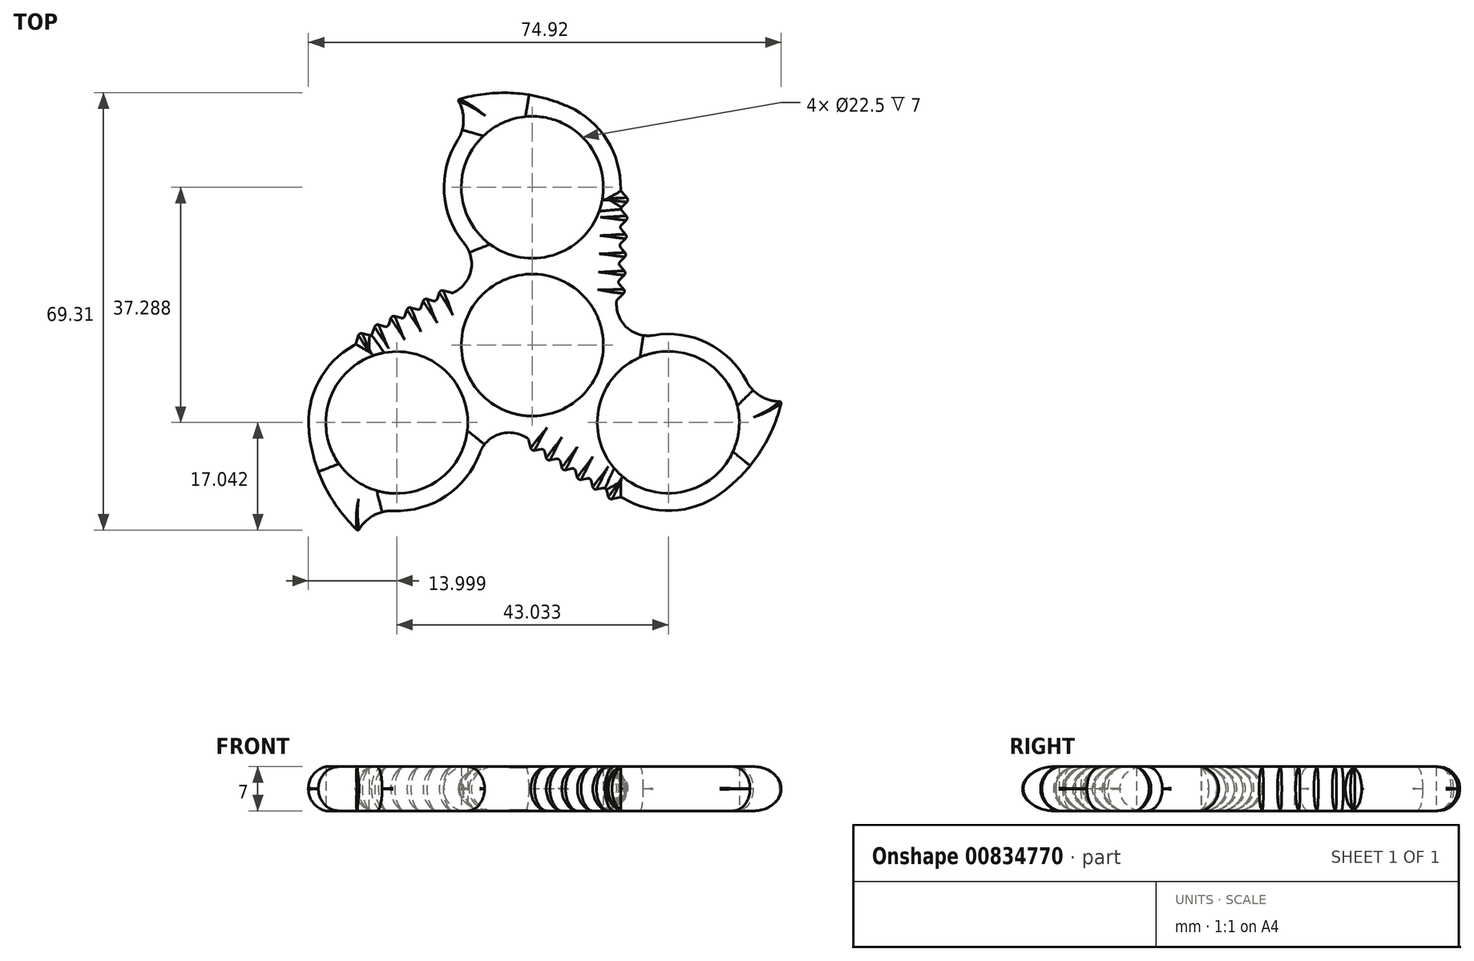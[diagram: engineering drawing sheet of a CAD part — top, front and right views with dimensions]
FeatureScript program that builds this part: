
annotation { "Feature Type Name" : "Feature", "Feature Type Description" : "" }
export const myFeature = defineFeature(function(context is Context, id is Id, definition is map)
    precondition{}
    {
        {
            var Q0;
            Q0=qCreatedBy(makeId("Top.planeOp"),FACE);
            var sketch = newSketch(context, id + "F0", { "sketchPlane" : qUnion([Q0])});
            skCircle(sketch, "E0", {"center": v(0, 0) * mm, "radius": 25 * mm, "construction": true});
            skCircle(sketch, "E1", {"center": v(0, 0) * mm, "radius": 11.25 * mm});
            skArc(sketch, "E2", {"start": v(14, 24.5) * mm, "mid": v(11.9, 32.39) * mm, "end": v(5.75, 37.77) * mm});
            skLineSegment(sketch, "E3", {"start": v(13.35, 6.66) * mm, "end": v(13.36, 7.1) * mm});
            skPoint(sketch, "E4.visualSharp", {"position": v(-4.7, 11.81) * mm});
            skArc(sketch, "E4.filletArc", {"start": v(-12.27, 8.44) * mm, "mid": v(-9.7, 11.89) * mm, "end": v(-10.77, 16.05) * mm});
            skPoint(sketch, "E5.visualSharp", {"position": v(13.05, -1.63) * mm});
            skArc(sketch, "E6", {"start": v(5.75, 37.77) * mm, "mid": v(-2.94, 39.93) * mm, "end": v(-11.83, 38.9) * mm});
            skArc(sketch, "E7", {"start": v(-11.83, 32.48) * mm, "mid": v(-10.9, 35.7) * mm, "end": v(-11.83, 38.9) * mm});
            skArc(sketch, "E8.trimOffspring", {"start": v(-11.83, 32.48) * mm, "mid": v(-13.97, 24.1) * mm, "end": v(-10.77, 16.05) * mm});
            skLineSegment(sketch, "E9", {"start": v(14, 24.5) * mm, "end": v(15.31, 23) * mm});
            skLineSegment(sketch, "E10", {"start": v(15.31, 23) * mm, "end": v(13.89, 21.6) * mm});
            skLineSegment(sketch, "E11.1.0.0", {"start": v(15.2, 20.1) * mm, "end": v(13.78, 18.7) * mm});
            skLineSegment(sketch, "E11.1.0.1", {"start": v(13.89, 21.6) * mm, "end": v(15.2, 20.1) * mm});
            skLineSegment(sketch, "E11.2.0.0", {"start": v(15.1, 17.2) * mm, "end": v(13.68, 15.8) * mm});
            skLineSegment(sketch, "E11.2.0.1", {"start": v(13.78, 18.7) * mm, "end": v(15.1, 17.2) * mm});
            skLineSegment(sketch, "E11.3.0.0", {"start": v(15, 14.3) * mm, "end": v(13.57, 12.9) * mm});
            skLineSegment(sketch, "E11.3.0.1", {"start": v(13.68, 15.8) * mm, "end": v(15, 14.3) * mm});
            skLineSegment(sketch, "E11.4.0.0", {"start": v(14.9, 11.4) * mm, "end": v(13.47, 10) * mm});
            skLineSegment(sketch, "E11.4.0.1", {"start": v(13.57, 12.9) * mm, "end": v(14.9, 11.4) * mm});
            skLineSegment(sketch, "E11.5.0.0", {"start": v(14.79, 8.5) * mm, "end": v(13.36, 7.1) * mm});
            skLineSegment(sketch, "E11.5.0.1", {"start": v(13.47, 10) * mm, "end": v(14.79, 8.5) * mm});
            skArc(sketch, "E12.1.0", {"start": v(-22.04, -26.28) * mm, "mid": v(-25.29, -27.08) * mm, "end": v(-27.6, -29.49) * mm});
            skArc(sketch, "E12.1.1", {"start": v(-1, -14.64) * mm, "mid": v(-5.27, -14.14) * mm, "end": v(-8.35, -17.14) * mm});
            skArc(sketch, "E12.1.2", {"start": v(-22.04, -26.28) * mm, "mid": v(-13.71, -23.93) * mm, "end": v(-8.35, -17.14) * mm});
            skArc(sketch, "E12.1.3", {"start": v(-35.41, -13.7) * mm, "mid": v(-32.94, -22.3) * mm, "end": v(-27.6, -29.49) * mm});
            skArc(sketch, "E12.1.4", {"start": v(-28.04, 0.08) * mm, "mid": v(-33.82, -5.68) * mm, "end": v(-35.41, -13.7) * mm});
            skLineSegment(sketch, "E12.1.6", {"start": v(-28.04, 0.08) * mm, "end": v(-27.4, 1.98) * mm});
            skLineSegment(sketch, "E12.1.7", {"start": v(-27.4, 1.98) * mm, "end": v(-25.47, 1.44) * mm});
            skLineSegment(sketch, "E12.1.8", {"start": v(-25.48, 1.44) * mm, "end": v(-24.84, 3.34) * mm});
            skLineSegment(sketch, "E12.1.9", {"start": v(-24.84, 3.34) * mm, "end": v(-22.91, 2.8) * mm});
            skLineSegment(sketch, "E12.1.10", {"start": v(-22.91, 2.8) * mm, "end": v(-22.28, 4.7) * mm});
            skLineSegment(sketch, "E12.1.11", {"start": v(-22.28, 4.7) * mm, "end": v(-20.35, 4.16) * mm});
            skLineSegment(sketch, "E12.1.12", {"start": v(-20.35, 4.16) * mm, "end": v(-19.71, 6.05) * mm});
            skLineSegment(sketch, "E12.1.13", {"start": v(-19.71, 6.05) * mm, "end": v(-17.79, 5.52) * mm});
            skLineSegment(sketch, "E12.1.14", {"start": v(-17.79, 5.51) * mm, "end": v(-17.15, 7.41) * mm});
            skLineSegment(sketch, "E12.1.15", {"start": v(-17.15, 7.41) * mm, "end": v(-15.23, 6.87) * mm});
            skLineSegment(sketch, "E12.1.16", {"start": v(-15.23, 6.87) * mm, "end": v(-14.59, 8.77) * mm});
            skLineSegment(sketch, "E12.1.17", {"start": v(-14.59, 8.77) * mm, "end": v(-12.66, 8.23) * mm});
            skLineSegment(sketch, "E12.1.18", {"start": v(-12.27, 8.44) * mm, "end": v(-12.66, 8.23) * mm});
            skArc(sketch, "E12.2.0", {"start": v(33.95, -5.74) * mm, "mid": v(36.26, -8.15) * mm, "end": v(39.5, -8.95) * mm});
            skArc(sketch, "E12.2.1", {"start": v(13.35, 6.66) * mm, "mid": v(15.05, 2.72) * mm, "end": v(19.19, 1.55) * mm});
            skArc(sketch, "E12.2.2", {"start": v(33.95, -5.74) * mm, "mid": v(27.75, 0.3) * mm, "end": v(19.19, 1.55) * mm});
            skArc(sketch, "E12.2.3", {"start": v(29.73, -23.6) * mm, "mid": v(35.95, -17.16) * mm, "end": v(39.5, -8.95) * mm});
            skArc(sketch, "E12.2.4", {"start": v(14.12, -24.11) * mm, "mid": v(22, -26.24) * mm, "end": v(29.73, -23.6) * mm});
            skLineSegment(sketch, "E12.2.6", {"start": v(14.12, -24.11) * mm, "end": v(12.16, -24.5) * mm});
            skLineSegment(sketch, "E12.2.7", {"start": v(12.16, -24.5) * mm, "end": v(11.66, -22.57) * mm});
            skLineSegment(sketch, "E12.2.8", {"start": v(11.66, -22.57) * mm, "end": v(9.7, -22.97) * mm});
            skLineSegment(sketch, "E12.2.9", {"start": v(9.7, -22.97) * mm, "end": v(9.2, -21.03) * mm});
            skLineSegment(sketch, "E12.2.10", {"start": v(9.2, -21.03) * mm, "end": v(7.24, -21.43) * mm});
            skLineSegment(sketch, "E12.2.11", {"start": v(7.24, -21.43) * mm, "end": v(6.74, -19.5) * mm});
            skLineSegment(sketch, "E12.2.12", {"start": v(6.75, -19.5) * mm, "end": v(4.79, -19.89) * mm});
            skLineSegment(sketch, "E12.2.13", {"start": v(4.79, -19.89) * mm, "end": v(4.29, -17.95) * mm});
            skLineSegment(sketch, "E12.2.14", {"start": v(4.29, -17.95) * mm, "end": v(2.33, -18.35) * mm});
            skLineSegment(sketch, "E12.2.15", {"start": v(2.33, -18.35) * mm, "end": v(1.83, -16.41) * mm});
            skLineSegment(sketch, "E12.2.16", {"start": v(1.83, -16.41) * mm, "end": v(-0.13, -16.8) * mm});
            skLineSegment(sketch, "E12.2.17", {"start": v(-0.13, -16.8) * mm, "end": v(-0.63, -14.87) * mm});
            skLineSegment(sketch, "E12.2.18", {"start": v(-1, -14.64) * mm, "end": v(-0.63, -14.87) * mm});
            skPoint(sketch, "E12.center", {"position": v(0.03, -3.97) * mm});
            skLineSegment(sketch, "E13.trimOffspring", {"start": v(-25.47, 1.44) * mm, "end": v(-25.48, 1.44) * mm});
            skLineSegment(sketch, "E14.trimOffspring", {"start": v(-22.91, 2.8) * mm, "end": v(-22.91, 2.8) * mm});
            skLineSegment(sketch, "E15.trimOffspring", {"start": v(-20.35, 4.16) * mm, "end": v(-20.35, 4.16) * mm});
            skLineSegment(sketch, "E16.trimOffspring", {"start": v(-17.79, 5.52) * mm, "end": v(-17.79, 5.51) * mm});
            skLineSegment(sketch, "E17.trimOffspring", {"start": v(-15.23, 6.87) * mm, "end": v(-15.23, 6.87) * mm});
            skLineSegment(sketch, "E18.trimOffspring", {"start": v(1.83, -16.41) * mm, "end": v(1.83, -16.41) * mm});
            skLineSegment(sketch, "E19.trimOffspring", {"start": v(4.29, -17.95) * mm, "end": v(4.29, -17.95) * mm});
            skLineSegment(sketch, "E20.trimOffspring", {"start": v(6.74, -19.5) * mm, "end": v(6.75, -19.5) * mm});
            skLineSegment(sketch, "E21.trimOffspring", {"start": v(9.2, -21.03) * mm, "end": v(9.2, -21.03) * mm});
            skLineSegment(sketch, "E22.trimOffspring", {"start": v(11.26, -22.32) * mm, "end": v(11.66, -22.57) * mm});
            skLineSegment(sketch, "E23.trimOffspring", {"start": v(13.47, 10) * mm, "end": v(13.47, 10) * mm});
            skLineSegment(sketch, "E24.trimOffspring", {"start": v(13.57, 12.9) * mm, "end": v(13.57, 12.9) * mm});
            skLineSegment(sketch, "E25.trimOffspring", {"start": v(13.68, 15.8) * mm, "end": v(13.68, 15.8) * mm});
            skLineSegment(sketch, "E26.trimOffspring", {"start": v(13.78, 18.7) * mm, "end": v(13.78, 18.7) * mm});
            skLineSegment(sketch, "E27.trimOffspring", {"start": v(13.78, 18.7) * mm, "end": v(13.78, 18.7) * mm, "construction": true});
            skLineSegment(sketch, "E28.trimOffspring", {"start": v(13.89, 21.6) * mm, "end": v(13.89, 21.6) * mm});
            skPoint(sketch, "E29.0.midPoint", {"position": v(13.99, -7.94) * mm});
            skLineSegment(sketch, "E30", {"start": v(0.03, -3.97) * mm, "end": v(0, 25) * mm});
            skCircle(sketch, "E31", {"center": v(-21.48, -12.29) * mm, "radius": 11.25 * mm});
            skCircle(sketch, "E32", {"center": v(0, 25) * mm, "radius": 11.25 * mm});
            skCircle(sketch, "E33", {"center": v(21.55, -12.25) * mm, "radius": 11.25 * mm});
            skSolve(sketch);
        }
        {
            var Q0;
            Q0=qSketchRegion(id+"F0",true);
            extrude(context, id + "F1", {"entities" : qUnion([Q0]), "depth" : 7 * mm, "offsetDistance" : 25 * mm});
        }
        {
            var Q0;
            Q0=makeQuery(id+"F1.opExtrude","SWEPT_EDGE",EDGE,{"disambiguationData":[OSD([sQuery(id+"F0.wireOp",EDGE,"E12.1.17"),sQuery(id+"F0.wireOp",EDGE,"E12.1.18")])]});
            var Q1;
            Q1=makeQuery(id+"F1.opExtrude","SWEPT_EDGE",EDGE,{"disambiguationData":[OSD([sQuery(id+"F0.wireOp",EDGE,"E12.1.16"),sQuery(id+"F0.wireOp",EDGE,"E12.1.17")])]});
            var Q2;
            Q2=makeQuery(id+"F1.opExtrude","SWEPT_EDGE",EDGE,{"disambiguationData":[OSD([sQuery(id+"F0.wireOp",EDGE,"E12.1.15"),sQuery(id+"F0.wireOp",EDGE,"E12.1.16")])]});
            var Q3;
            Q3=makeQuery(id+"F1.opExtrude","SWEPT_EDGE",EDGE,{"disambiguationData":[OSD([sQuery(id+"F0.wireOp",EDGE,"E12.1.14"),sQuery(id+"F0.wireOp",EDGE,"E12.1.15")])]});
            var Q4;
            Q4=makeQuery(id+"F1.opExtrude","SWEPT_EDGE",EDGE,{"disambiguationData":[OSD([sQuery(id+"F0.wireOp",EDGE,"E12.1.13"),sQuery(id+"F0.wireOp",EDGE,"E12.1.14")])]});
            var Q5;
            Q5=makeQuery(id+"F1.opExtrude","SWEPT_EDGE",EDGE,{"disambiguationData":[OSD([sQuery(id+"F0.wireOp",EDGE,"E12.1.12"),sQuery(id+"F0.wireOp",EDGE,"E12.1.13")])]});
            var Q6;
            Q6=makeQuery(id+"F1.opExtrude","SWEPT_EDGE",EDGE,{"disambiguationData":[OSD([sQuery(id+"F0.wireOp",EDGE,"E12.1.11"),sQuery(id+"F0.wireOp",EDGE,"E12.1.12")])]});
            var Q7;
            Q7=makeQuery(id+"F1.opExtrude","SWEPT_EDGE",EDGE,{"disambiguationData":[OSD([sQuery(id+"F0.wireOp",EDGE,"E12.1.10"),sQuery(id+"F0.wireOp",EDGE,"E12.1.11")])]});
            var Q8;
            Q8=makeQuery(id+"F1.opExtrude","SWEPT_EDGE",EDGE,{"disambiguationData":[OSD([sQuery(id+"F0.wireOp",EDGE,"E12.1.9"),sQuery(id+"F0.wireOp",EDGE,"E12.1.10")])]});
            var Q9;
            Q9=makeQuery(id+"F1.opExtrude","SWEPT_EDGE",EDGE,{"disambiguationData":[OSD([sQuery(id+"F0.wireOp",EDGE,"E12.1.8"),sQuery(id+"F0.wireOp",EDGE,"E12.1.9")])]});
            var Q10;
            Q10=makeQuery(id+"F1.opExtrude","SWEPT_EDGE",EDGE,{"disambiguationData":[OSD([sQuery(id+"F0.wireOp",EDGE,"E12.1.7"),sQuery(id+"F0.wireOp",EDGE,"E12.1.8")])]});
            var Q11;
            Q11=makeQuery(id+"F1.opExtrude","SWEPT_EDGE",EDGE,{"disambiguationData":[OSD([sQuery(id+"F0.wireOp",EDGE,"E12.1.6"),sQuery(id+"F0.wireOp",EDGE,"E12.1.7")])]});
            var Q12;
            Q12=makeQuery(id+"F1.opExtrude","SWEPT_EDGE",EDGE,{"disambiguationData":[OSD([sQuery(id+"F0.wireOp",EDGE,"E12.1.4"),sQuery(id+"F0.wireOp",EDGE,"E12.1.6")])]});
            var Q13;
            Q13=makeQuery(id+"F1.opExtrude","SWEPT_EDGE",EDGE,{"disambiguationData":[OSD([sQuery(id+"F0.wireOp",EDGE,"E12.2.17"),sQuery(id+"F0.wireOp",EDGE,"E12.2.18")])]});
            var Q14;
            Q14=makeQuery(id+"F1.opExtrude","SWEPT_EDGE",EDGE,{"disambiguationData":[OSD([sQuery(id+"F0.wireOp",EDGE,"E12.2.16"),sQuery(id+"F0.wireOp",EDGE,"E12.2.17")])]});
            var Q15;
            Q15=makeQuery(id+"F1.opExtrude","SWEPT_EDGE",EDGE,{"disambiguationData":[OSD([sQuery(id+"F0.wireOp",EDGE,"E12.2.15"),sQuery(id+"F0.wireOp",EDGE,"E12.2.16")])]});
            var Q16;
            Q16=makeQuery(id+"F1.opExtrude","SWEPT_EDGE",EDGE,{"disambiguationData":[OSD([sQuery(id+"F0.wireOp",EDGE,"E12.2.14"),sQuery(id+"F0.wireOp",EDGE,"E12.2.15")])]});
            var Q17;
            Q17=makeQuery(id+"F1.opExtrude","SWEPT_EDGE",EDGE,{"disambiguationData":[OSD([sQuery(id+"F0.wireOp",EDGE,"E12.2.13"),sQuery(id+"F0.wireOp",EDGE,"E12.2.14")])]});
            var Q18;
            Q18=makeQuery(id+"F1.opExtrude","SWEPT_EDGE",EDGE,{"disambiguationData":[OSD([sQuery(id+"F0.wireOp",EDGE,"E12.2.12"),sQuery(id+"F0.wireOp",EDGE,"E12.2.13")])]});
            var Q19;
            Q19=makeQuery(id+"F1.opExtrude","SWEPT_EDGE",EDGE,{"disambiguationData":[OSD([sQuery(id+"F0.wireOp",EDGE,"E12.2.11"),sQuery(id+"F0.wireOp",EDGE,"E12.2.12")])]});
            var Q20;
            Q20=makeQuery(id+"F1.opExtrude","SWEPT_EDGE",EDGE,{"disambiguationData":[OSD([sQuery(id+"F0.wireOp",EDGE,"E12.2.10"),sQuery(id+"F0.wireOp",EDGE,"E12.2.11")])]});
            var Q21;
            Q21=makeQuery(id+"F1.opExtrude","SWEPT_EDGE",EDGE,{"disambiguationData":[OSD([sQuery(id+"F0.wireOp",EDGE,"E12.2.9"),sQuery(id+"F0.wireOp",EDGE,"E12.2.10")])]});
            var Q22;
            Q22=makeQuery(id+"F1.opExtrude","SWEPT_EDGE",EDGE,{"disambiguationData":[OSD([sQuery(id+"F0.wireOp",EDGE,"E12.2.8"),sQuery(id+"F0.wireOp",EDGE,"E12.2.9")])]});
            var Q23;
            Q23=makeQuery(id+"F1.opExtrude","SWEPT_EDGE",EDGE,{"disambiguationData":[OSD([sQuery(id+"F0.wireOp",EDGE,"E12.2.7"),sQuery(id+"F0.wireOp",EDGE,"E12.2.8")])]});
            var Q24;
            Q24=makeQuery(id+"F1.opExtrude","SWEPT_EDGE",EDGE,{"disambiguationData":[OSD([sQuery(id+"F0.wireOp",EDGE,"E12.2.6"),sQuery(id+"F0.wireOp",EDGE,"E12.2.7")])]});
            var Q25;
            Q25=makeQuery(id+"F1.opExtrude","SWEPT_EDGE",EDGE,{"disambiguationData":[OSD([sQuery(id+"F0.wireOp",EDGE,"E12.2.4"),sQuery(id+"F0.wireOp",EDGE,"E12.2.6")])]});
            var Q26;
            Q26=makeQuery(id+"F1.opExtrude","SWEPT_EDGE",EDGE,{"disambiguationData":[OSD([sQuery(id+"F0.wireOp",EDGE,"E2"),sQuery(id+"F0.wireOp",EDGE,"E9")])]});
            var Q27;
            Q27=makeQuery(id+"F1.opExtrude","SWEPT_EDGE",EDGE,{"disambiguationData":[OSD([sQuery(id+"F0.wireOp",EDGE,"E9"),sQuery(id+"F0.wireOp",EDGE,"E10")])]});
            var Q28;
            Q28=makeQuery(id+"F1.opExtrude","SWEPT_EDGE",EDGE,{"disambiguationData":[OSD([sQuery(id+"F0.wireOp",EDGE,"E10"),sQuery(id+"F0.wireOp",EDGE,"E11.1.0.1")])]});
            var Q29;
            Q29=makeQuery(id+"F1.opExtrude","SWEPT_EDGE",EDGE,{"disambiguationData":[OSD([sQuery(id+"F0.wireOp",EDGE,"E11.1.0.0"),sQuery(id+"F0.wireOp",EDGE,"E11.1.0.1")])]});
            var Q30;
            Q30=makeQuery(id+"F1.opExtrude","SWEPT_EDGE",EDGE,{"disambiguationData":[OSD([sQuery(id+"F0.wireOp",EDGE,"E11.1.0.0"),sQuery(id+"F0.wireOp",EDGE,"E11.2.0.1")])]});
            var Q31;
            Q31=makeQuery(id+"F1.opExtrude","SWEPT_EDGE",EDGE,{"disambiguationData":[OSD([sQuery(id+"F0.wireOp",EDGE,"E11.2.0.0"),sQuery(id+"F0.wireOp",EDGE,"E11.2.0.1")])]});
            var Q32;
            Q32=makeQuery(id+"F1.opExtrude","SWEPT_EDGE",EDGE,{"disambiguationData":[OSD([sQuery(id+"F0.wireOp",EDGE,"E11.2.0.0"),sQuery(id+"F0.wireOp",EDGE,"E11.3.0.1")])]});
            var Q33;
            Q33=makeQuery(id+"F1.opExtrude","SWEPT_EDGE",EDGE,{"disambiguationData":[OSD([sQuery(id+"F0.wireOp",EDGE,"E11.3.0.0"),sQuery(id+"F0.wireOp",EDGE,"E11.3.0.1")])]});
            var Q34;
            Q34=makeQuery(id+"F1.opExtrude","SWEPT_EDGE",EDGE,{"disambiguationData":[OSD([sQuery(id+"F0.wireOp",EDGE,"E11.3.0.0"),sQuery(id+"F0.wireOp",EDGE,"E11.4.0.1")])]});
            var Q35;
            Q35=makeQuery(id+"F1.opExtrude","SWEPT_EDGE",EDGE,{"disambiguationData":[OSD([sQuery(id+"F0.wireOp",EDGE,"E11.4.0.0"),sQuery(id+"F0.wireOp",EDGE,"E11.4.0.1")])]});
            var Q36;
            Q36=makeQuery(id+"F1.opExtrude","SWEPT_EDGE",EDGE,{"disambiguationData":[OSD([sQuery(id+"F0.wireOp",EDGE,"E11.4.0.0"),sQuery(id+"F0.wireOp",EDGE,"E11.5.0.1")])]});
            var Q37;
            Q37=makeQuery(id+"F1.opExtrude","SWEPT_EDGE",EDGE,{"disambiguationData":[OSD([sQuery(id+"F0.wireOp",EDGE,"E11.5.0.0"),sQuery(id+"F0.wireOp",EDGE,"E11.5.0.1")])]});
            var Q38;
            Q38=makeQuery(id+"F1.opExtrude","SWEPT_EDGE",EDGE,{"disambiguationData":[OSD([sQuery(id+"F0.wireOp",EDGE,"E3"),sQuery(id+"F0.wireOp",EDGE,"E11.5.0.0")])]});
            fillet(context, id + "F2", {"entities" : qUnion([Q0, Q1, Q2, Q3, Q4, Q5, Q6, Q7, Q8, Q9, Q10, Q11, Q12, Q13, Q14, Q15, Q16, Q17, Q18, Q19, Q20, Q21, Q22, Q23, Q24, Q25, Q26, Q27, Q28, Q29, Q30, Q31, Q32, Q33, Q34, Q35, Q36, Q37, Q38]), "radius" : .5 * mm, "tangentPropagation" : true, "allowEdgeOverflow" : false});
        }
        {
            var Q0;
            Q0=makeQuery(id+"F1.opExtrude","SWEPT_EDGE",EDGE,{"disambiguationData":[OSD([sQuery(id+"F0.wireOp",EDGE,"E6"),sQuery(id+"F0.wireOp",EDGE,"E7")])]});
            var Q1;
            Q1=makeQuery(id+"F1.opExtrude","SWEPT_EDGE",EDGE,{"disambiguationData":[OSD([sQuery(id+"F0.wireOp",EDGE,"E12.1.0"),sQuery(id+"F0.wireOp",EDGE,"E12.1.3")])]});
            var Q2;
            Q2=makeQuery(id+"F1.opExtrude","SWEPT_EDGE",EDGE,{"disambiguationData":[OSD([sQuery(id+"F0.wireOp",EDGE,"E12.2.0"),sQuery(id+"F0.wireOp",EDGE,"E12.2.3")])]});
            fillet(context, id + "F3", {"entities" : qUnion([Q0, Q1, Q2]), "radius" : .25 * mm, "tangentPropagation" : true, "allowEdgeOverflow" : false});
        }
        {
            var Q0;
            Q0=makeQuery(id+"F1.opExtrude","CAP_EDGE",EDGE,{"disambiguationData":[OSD([sQuery(id+"F0.wireOp",EDGE,"E12.2.4")])],"isStart":false});
            var Q1;
            Q1=makeQuery(id+"F1.opExtrude","CAP_EDGE",EDGE,{"disambiguationData":[OSD([sQuery(id+"F0.wireOp",EDGE,"E12.1.1")])],"isStart":true});
            fillet(context, id + "F4", {"entities" : qUnion([Q0, Q1]), "radius" : 3.5 * mm, "tangentPropagation" : true, "allowEdgeOverflow" : false});
        }
    });
